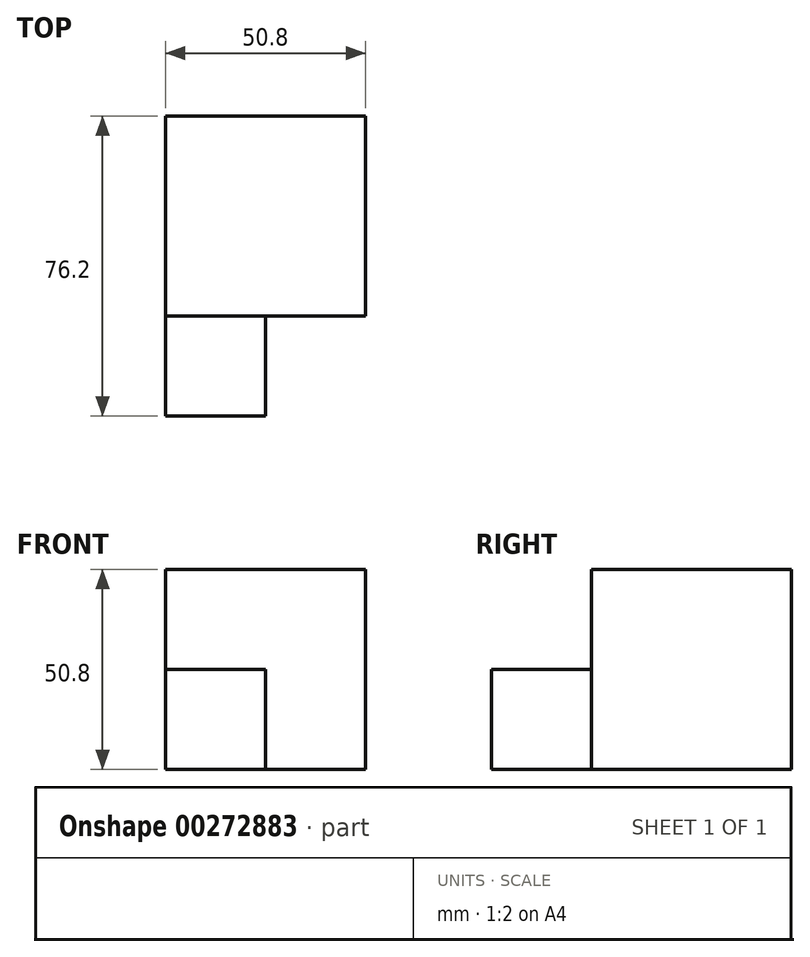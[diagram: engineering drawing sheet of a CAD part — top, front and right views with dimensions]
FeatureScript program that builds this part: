
annotation { "Feature Type Name" : "Feature", "Feature Type Description" : "" }
export const myFeature = defineFeature(function(context is Context, id is Id, definition is map)
    precondition{}
    {
        {
            var Q0;
            Q0=qCreatedBy(makeId("Front.planeOp"),FACE);
            var sketch = newSketch(context, id + "F0", { "sketchPlane" : qUnion([Q0])});
            skLineSegment(sketch, "E0", {"start": v(0, 0) * mm, "end": v(-50.8, 0) * mm});
            skLineSegment(sketch, "E1", {"start": v(-50.8, 0) * mm, "end": v(-50.8, 50.8) * mm});
            skLineSegment(sketch, "E2", {"start": v(-50.8, 50.8) * mm, "end": v(0, 50.8) * mm});
            skLineSegment(sketch, "E3", {"start": v(0, 50.8) * mm, "end": v(0, 0) * mm});
            skSolve(sketch);
        }
        {
            var Q0;
            Q0=makeQuery(id+"F0.imprint","IMPRINT",FACE,{"disambiguationData":[TD([[makeQuery(id+"F0.imprint","IMPRINT",EDGE,{"derivedFrom":sQuery(id+"F0.wireOp",EDGE,"E0")}),-1.0]])]});
            extrude(context, id + "F1", {"entities" : qUnion([Q0]), "depth" : 50.8 * mm});
        }
        {
            var Q0;
            Q0=makeQuery(id+"F1.opExtrude","CAP_FACE",FACE,{"disambiguationData":[OSD([sQuery(id+"F0.wireOp",EDGE,"E0"),sQuery(id+"F0.wireOp",EDGE,"E1"),sQuery(id+"F0.wireOp",EDGE,"E2"),sQuery(id+"F0.wireOp",EDGE,"E3")])],"isStart":false});
            var sketch = newSketch(context, id + "F2", { "sketchPlane" : qUnion([Q0])});
            skLineSegment(sketch, "E4", {"start": v(-50.8, 25.4) * mm, "end": v(-25.4, 25.4) * mm});
            skLineSegment(sketch, "E5", {"start": v(-25.4, 25.4) * mm, "end": v(-25.4, 0) * mm});
            skLineSegment(sketch, "E6", {"start": v(-50.8, 25.4) * mm, "end": v(-50.8, 0) * mm});
            skLineSegment(sketch, "E7", {"start": v(-50.8, 0) * mm, "end": v(-25.4, 0) * mm});
            skSolve(sketch);
        }
        {
            var Q0;
            Q0 = qSketchRegion(id + "F2", true);
            extrude(context, id + "F3", {"entities" : qUnion([Q0]), "operationType" : NewBodyOperationType.ADD, "depth" : 25.4 * mm});
        }
    });
